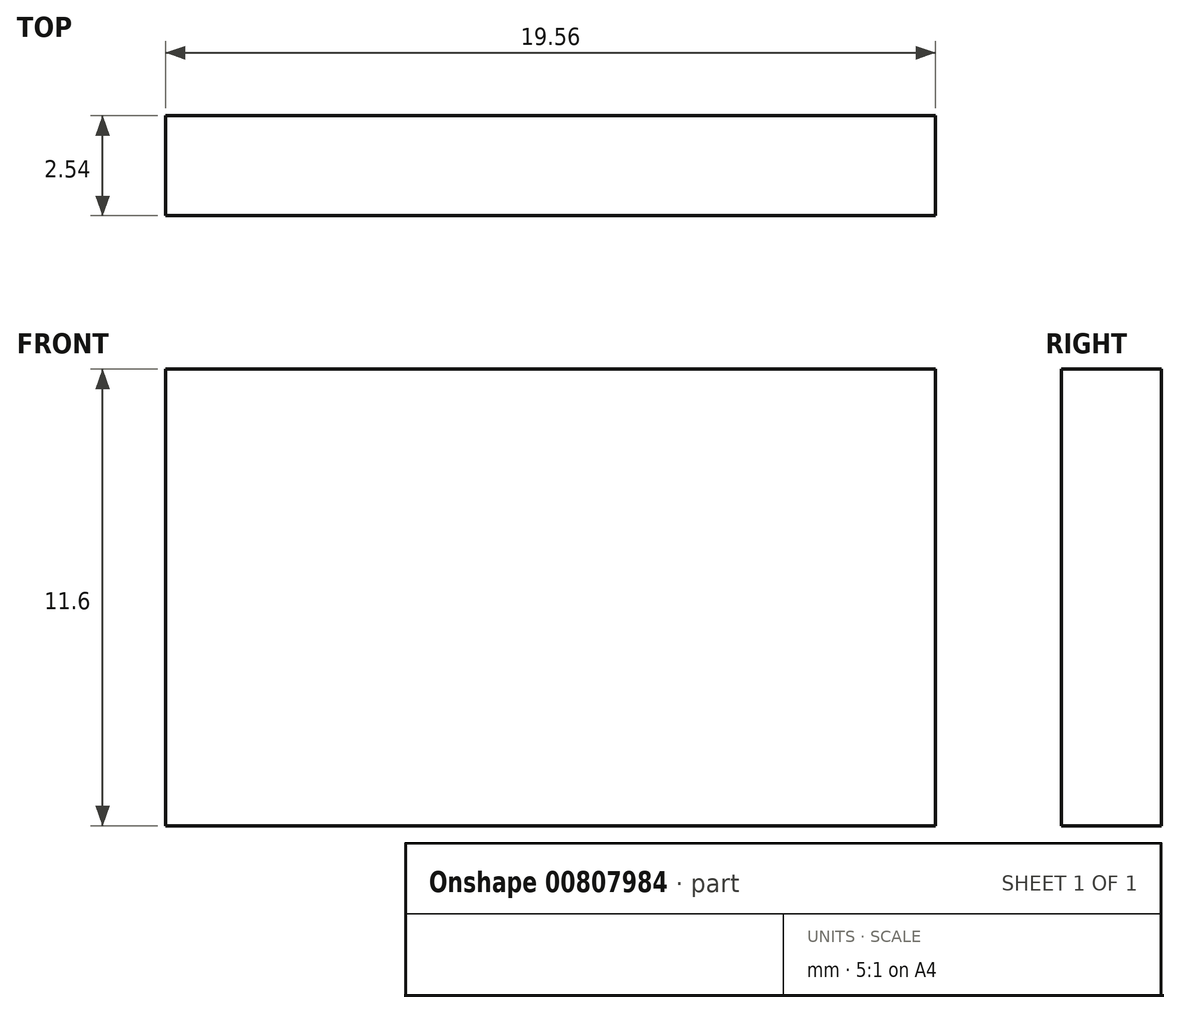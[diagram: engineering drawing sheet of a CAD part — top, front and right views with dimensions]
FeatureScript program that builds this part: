
annotation { "Feature Type Name" : "Feature", "Feature Type Description" : "" }
export const myFeature = defineFeature(function(context is Context, id is Id, definition is map)
    precondition{}
    {
        {
            var Q0;
            Q0=qCreatedBy(makeId("Front.planeOp"),FACE);
            var sketch = newSketch(context, id + "F0", { "sketchPlane" : qUnion([Q0])});
            skLineSegment(sketch, "E0.bottom", {"start": v(-9.78, -19.22) * mm, "end": v(0, -19.22) * mm});
            skLineSegment(sketch, "E0.top", {"start": v(-9.78, -30.82) * mm, "end": v(0, -30.82) * mm});
            skLineSegment(sketch, "E0.left", {"start": v(-9.78, -19.22) * mm, "end": v(-9.78, -30.82) * mm});
            skLineSegment(sketch, "E0.right", {"start": v(0, -19.22) * mm, "end": v(0, -30.82) * mm});
            skLineSegment(sketch, "E1.MirrorCS", {"start": v(9.78, -30.82) * mm, "end": v(0, -30.82) * mm});
            skLineSegment(sketch, "E2.MirrorCS", {"start": v(9.78, -19.22) * mm, "end": v(9.78, -30.82) * mm});
            skLineSegment(sketch, "E3.MirrorCS", {"start": v(9.78, -19.22) * mm, "end": v(0, -19.22) * mm});
            skSolve(sketch);
        }
        {
            var Q0;
            Q0=makeQuery(id+"F0.imprint","IMPRINT",FACE,{"disambiguationData":[TD([[makeQuery(id+"F0.imprint","IMPRINT",EDGE,{"derivedFrom":sQuery(id+"F0.wireOp",EDGE,"E0.right")}),1.0]])]});
            var Q1;
            Q1=makeQuery(id+"F0.imprint","IMPRINT",FACE,{"disambiguationData":[TD([[makeQuery(id+"F0.imprint","IMPRINT",EDGE,{"derivedFrom":sQuery(id+"F0.wireOp",EDGE,"E0.bottom")}),-1.0]])]});
            extrude(context, id + "F1", {"entities" : qUnion([Q0, Q1]), "oppositeDirection" : true, "depth" : 2.54 * mm, "offsetDistance" : 25.4 * mm});
        }
    });
